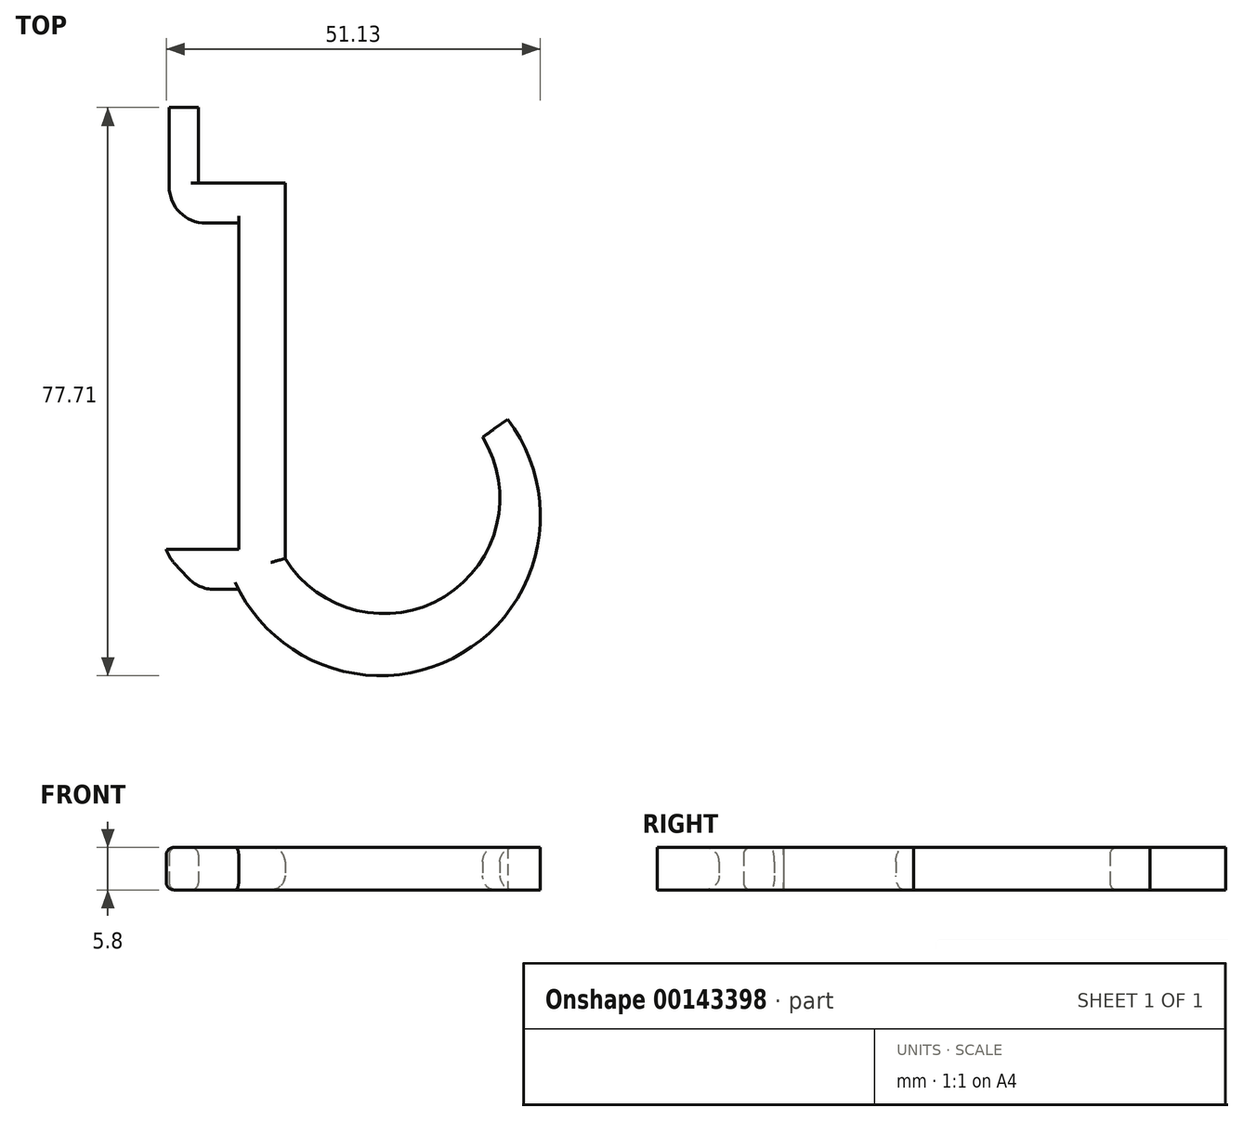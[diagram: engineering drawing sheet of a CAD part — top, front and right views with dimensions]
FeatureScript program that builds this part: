
annotation { "Feature Type Name" : "Feature", "Feature Type Description" : "" }
export const myFeature = defineFeature(function(context is Context, id is Id, definition is map)
    precondition{}
    {
        {
            var Q0;
            Q0=qCreatedBy(makeId("Top.planeOp"),FACE);
            var sketch = newSketch(context, id + "F0", { "sketchPlane" : qUnion([Q0])});
            skLineSegment(sketch, "E0.top", {"start": v(0, 55.6) * mm, "end": v(6.35, 55.6) * mm});
            skLineSegment(sketch, "E0.left", {"start": v(0, 0) * mm, "end": v(0, 55.6) * mm});
            skLineSegment(sketch, "E0.right", {"start": v(6.35, 4.23) * mm, "end": v(6.35, 55.6) * mm});
            skArc(sketch, "E1", {"start": v(0, 0) * mm, "mid": v(31.07, -8.42) * mm, "end": v(36.78, 23.26) * mm});
            skArc(sketch, "E2", {"start": v(6.35, 4.23) * mm, "mid": v(28.16, -0.98) * mm, "end": v(33.37, 20.82) * mm});
            skLineSegment(sketch, "E3", {"start": v(33.37, 20.82) * mm, "end": v(36.78, 23.26) * mm});
            skLineSegment(sketch, "E4", {"start": v(0, 55.6) * mm, "end": v(-5.5, 55.6) * mm});
            skPoint(sketch, "E5.start.orphan", {"position": v(-5.5, 50.1) * mm});
            skLineSegment(sketch, "E6", {"start": v(-5.5, 50.1) * mm, "end": v(0, 50.1) * mm});
            skLineSegment(sketch, "E7", {"start": v(0, 27.8) * mm, "end": v(33.38, 27.8) * mm, "construction": true});
            skLineSegment(sketch, "E8", {"start": v(33.38, 27.8) * mm, "end": v(-54.11, 27.8) * mm, "construction": true});
            skLineSegment(sketch, "E9.MirrorCS", {"start": v(0, 0) * mm, "end": v(-5.5, 0) * mm});
            skLineSegment(sketch, "E10.MirrorCS", {"start": v(-5.5, 5.5) * mm, "end": v(0, 5.5) * mm});
            skPoint(sketch, "E11.MirrorCS.end.orphan", {"position": v(-5.5, 5.5) * mm});
            skPoint(sketch, "E11.MirrorCS.start.orphan", {"position": v(-12.78, -1.43) * mm});
            skPoint(sketch, "E12.MirrorCS.start.orphan", {"position": v(-12.78, -7.8) * mm});
            skPoint(sketch, "E13.MirrorCS.start.orphan", {"position": v(-5.5, 0) * mm});
            skLineSegment(sketch, "E14", {"start": v(-5.5, 55.6) * mm, "end": v(-5.5, 65.91) * mm});
            skLineSegment(sketch, "E15", {"start": v(-5.5, 65.91) * mm, "end": v(-9.5, 65.91) * mm});
            skLineSegment(sketch, "E16", {"start": v(-9.5, 65.91) * mm, "end": v(-9.5, 50.1) * mm});
            skLineSegment(sketch, "E17", {"start": v(-9.5, 50.1) * mm, "end": v(-5.5, 50.1) * mm});
            skPoint(sketch, "E18.start.orphan", {"position": v(-12.78, 63.4) * mm});
            skPoint(sketch, "E19.start.orphan", {"position": v(-12.78, 57.03) * mm});
            skPoint(sketch, "E20.end.orphan", {"position": v(-26.56, 0) * mm});
            skLineSegment(sketch, "E21", {"start": v(0, 50.1) * mm, "end": v(0, 55.6) * mm, "construction": true});
            skLineSegment(sketch, "E22", {"start": v(0, 52.85) * mm, "end": v(-28.66, 52.85) * mm, "construction": true});
            skPoint(sketch, "E22.endSnap0", {"position": v(0, 52.85) * mm});
            skLineSegment(sketch, "E23", {"start": v(0, 5.5) * mm, "end": v(0, 0) * mm, "construction": true});
            skLineSegment(sketch, "E24", {"start": v(0, 2.75) * mm, "end": v(-28.66, 2.75) * mm, "construction": true});
            skLineSegment(sketch, "E25", {"start": v(-28.66, 2.75) * mm, "end": v(-28.66, 52.85) * mm, "construction": true});
            skLineSegment(sketch, "E26", {"start": v(-5.5, 5.5) * mm, "end": v(-5.5, 16.71) * mm});
            skLineSegment(sketch, "E27", {"start": v(-5.5, 16.71) * mm, "end": v(-10.12, 16.71) * mm});
            skLineSegment(sketch, "E28", {"start": v(-10.12, 16.71) * mm, "end": v(-10.12, 5) * mm});
            skLineSegment(sketch, "E29", {"start": v(-10.12, 5) * mm, "end": v(-5.5, 0) * mm});
            skSolve(sketch);
        }
        {
            var Q0;
            Q0 = qSketchRegion(id + "F0", true);
            extrude(context, id + "F1", {"entities" : qUnion([Q0]), "depth" : 5.8 * mm});
        }
        {
            var Q0;
            Q0=makeQuery(id+"F1.opExtrude","SWEPT_EDGE",EDGE,{"disambiguationData":[OSD([sQuery(id+"F0.wireOp",EDGE,"E16"),sQuery(id+"F0.wireOp",EDGE,"E17")])]});
            fillet(context, id + "F2", {"entities" : qUnion([Q0]), "radius" : 5 * mm, "tangentPropagation" : true, "allowEdgeOverflow" : false});
        }
        {
            var Q0;
            Q0=makeQuery(id+"F1.opExtrude","SWEPT_EDGE",EDGE,{"disambiguationData":[OSD([sQuery(id+"F0.wireOp",EDGE,"E28"),sQuery(id+"F0.wireOp",EDGE,"E29")])]});
            var Q1;
            Q1=makeQuery(id+"F1.opExtrude","SWEPT_EDGE",EDGE,{"disambiguationData":[OSD([sQuery(id+"F0.wireOp",EDGE,"E9.MirrorCS"),sQuery(id+"F0.wireOp",EDGE,"E29")])]});
            fillet(context, id + "F3", {"entities" : qUnion([Q0, Q1]), "radius" : 5 * mm, "tangentPropagation" : true, "allowEdgeOverflow" : false});
        }
        {
            var Q0;
            Q0=makeQuery(id+"F1.opExtrude","CAP_EDGE",EDGE,{"disambiguationData":[OSD([sQuery(id+"F0.wireOp",EDGE,"E0.right")])],"isStart":true});
            var Q1;
            Q1=makeQuery(id+"F1.opExtrude","CAP_EDGE",EDGE,{"disambiguationData":[OSD([sQuery(id+"F0.wireOp",EDGE,"E0.right")])],"isStart":false});
            var Q2;
            Q2=makeQuery(id+"F1.opExtrude","CAP_EDGE",EDGE,{"disambiguationData":[OSD([sQuery(id+"F0.wireOp",EDGE,"E2")])],"isStart":false});
            var Q3;
            Q3=makeQuery(id+"F1.opExtrude","CAP_EDGE",EDGE,{"disambiguationData":[OSD([sQuery(id+"F0.wireOp",EDGE,"E2")])],"isStart":true});
            fillet(context, id + "F4", {"entities" : qUnion([Q0, Q1, Q2, Q3]), "radius" : 1.96 * mm, "tangentPropagation" : true, "allowEdgeOverflow" : false});
        }
        {
            var Q0;
            Q0=makeQuery(id+"F1.opExtrude","CAP_EDGE",EDGE,{"disambiguationData":[OSD([sQuery(id+"F0.wireOp",EDGE,"E26")])],"isStart":false});
            var Q1;
            Q1=makeQuery(id+"F1.opExtrude","CAP_EDGE",EDGE,{"disambiguationData":[OSD([sQuery(id+"F0.wireOp",EDGE,"E26")])],"isStart":true});
            var Q2;
            Q2=makeQuery(id+"F1.opExtrude","CAP_EDGE",EDGE,{"disambiguationData":[OSD([sQuery(id+"F0.wireOp",EDGE,"E28")])],"isStart":false});
            var Q3;
            Q3=makeQuery(id+"F1.opExtrude","CAP_EDGE",EDGE,{"disambiguationData":[OSD([sQuery(id+"F0.wireOp",EDGE,"E28")])],"isStart":true});
            var Q4;
            {var subQ0=sQuery(id+"F0.wireOp",EDGE,"E29");var subQ1=sQuery(id+"F0.wireOp",EDGE,"E28");Q4=makeQuery(id+"F3.opFillet","BLEND_EDGE",EDGE,{"blendedFrom":[makeQuery(id+"F1.opExtrude","SWEPT_EDGE",EDGE,{"disambiguationData":[OSD([subQ1,subQ0])]}),makeQuery(id+"F1.opExtrude","CAP_FACE",FACE,{"disambiguationData":[OSD([sQuery(id+"F0.wireOp",EDGE,"E0.top"),sQuery(id+"F0.wireOp",EDGE,"E0.left"),sQuery(id+"F0.wireOp",EDGE,"E0.right"),sQuery(id+"F0.wireOp",EDGE,"E1"),sQuery(id+"F0.wireOp",EDGE,"E2"),sQuery(id+"F0.wireOp",EDGE,"E3"),sQuery(id+"F0.wireOp",EDGE,"E4"),sQuery(id+"F0.wireOp",EDGE,"E6"),sQuery(id+"F0.wireOp",EDGE,"E10.MirrorCS"),sQuery(id+"F0.wireOp",EDGE,"E9.MirrorCS"),sQuery(id+"F0.wireOp",EDGE,"E14"),sQuery(id+"F0.wireOp",EDGE,"E15"),sQuery(id+"F0.wireOp",EDGE,"E16"),sQuery(id+"F0.wireOp",EDGE,"E17"),sQuery(id+"F0.wireOp",EDGE,"E26"),sQuery(id+"F0.wireOp",EDGE,"E27"),subQ1,subQ0])],"isStart":true})],"blendedInto":[makeQuery(id+"F1.opExtrude","CAP_FACE",FACE,{"disambiguationData":[OSD([sQuery(id+"F0.wireOp",EDGE,"E0.top"),sQuery(id+"F0.wireOp",EDGE,"E0.left"),sQuery(id+"F0.wireOp",EDGE,"E0.right"),sQuery(id+"F0.wireOp",EDGE,"E1"),sQuery(id+"F0.wireOp",EDGE,"E2"),sQuery(id+"F0.wireOp",EDGE,"E3"),sQuery(id+"F0.wireOp",EDGE,"E4"),sQuery(id+"F0.wireOp",EDGE,"E6"),sQuery(id+"F0.wireOp",EDGE,"E10.MirrorCS"),sQuery(id+"F0.wireOp",EDGE,"E9.MirrorCS"),sQuery(id+"F0.wireOp",EDGE,"E14"),sQuery(id+"F0.wireOp",EDGE,"E15"),sQuery(id+"F0.wireOp",EDGE,"E16"),sQuery(id+"F0.wireOp",EDGE,"E17"),sQuery(id+"F0.wireOp",EDGE,"E26"),sQuery(id+"F0.wireOp",EDGE,"E27"),subQ1,subQ0])],"isStart":true})]});}
            var Q5;
            {var subQ0=sQuery(id+"F0.wireOp",EDGE,"E29");var subQ1=sQuery(id+"F0.wireOp",EDGE,"E28");Q5=makeQuery(id+"F3.opFillet","BLEND_EDGE",EDGE,{"blendedFrom":[makeQuery(id+"F1.opExtrude","SWEPT_EDGE",EDGE,{"disambiguationData":[OSD([subQ1,subQ0])]}),makeQuery(id+"F1.opExtrude","CAP_FACE",FACE,{"disambiguationData":[OSD([sQuery(id+"F0.wireOp",EDGE,"E0.top"),sQuery(id+"F0.wireOp",EDGE,"E0.left"),sQuery(id+"F0.wireOp",EDGE,"E0.right"),sQuery(id+"F0.wireOp",EDGE,"E1"),sQuery(id+"F0.wireOp",EDGE,"E2"),sQuery(id+"F0.wireOp",EDGE,"E3"),sQuery(id+"F0.wireOp",EDGE,"E4"),sQuery(id+"F0.wireOp",EDGE,"E6"),sQuery(id+"F0.wireOp",EDGE,"E10.MirrorCS"),sQuery(id+"F0.wireOp",EDGE,"E9.MirrorCS"),sQuery(id+"F0.wireOp",EDGE,"E14"),sQuery(id+"F0.wireOp",EDGE,"E15"),sQuery(id+"F0.wireOp",EDGE,"E16"),sQuery(id+"F0.wireOp",EDGE,"E17"),sQuery(id+"F0.wireOp",EDGE,"E26"),sQuery(id+"F0.wireOp",EDGE,"E27"),subQ1,subQ0])],"isStart":false})],"blendedInto":[makeQuery(id+"F1.opExtrude","CAP_FACE",FACE,{"disambiguationData":[OSD([sQuery(id+"F0.wireOp",EDGE,"E0.top"),sQuery(id+"F0.wireOp",EDGE,"E0.left"),sQuery(id+"F0.wireOp",EDGE,"E0.right"),sQuery(id+"F0.wireOp",EDGE,"E1"),sQuery(id+"F0.wireOp",EDGE,"E2"),sQuery(id+"F0.wireOp",EDGE,"E3"),sQuery(id+"F0.wireOp",EDGE,"E4"),sQuery(id+"F0.wireOp",EDGE,"E6"),sQuery(id+"F0.wireOp",EDGE,"E10.MirrorCS"),sQuery(id+"F0.wireOp",EDGE,"E9.MirrorCS"),sQuery(id+"F0.wireOp",EDGE,"E14"),sQuery(id+"F0.wireOp",EDGE,"E15"),sQuery(id+"F0.wireOp",EDGE,"E16"),sQuery(id+"F0.wireOp",EDGE,"E17"),sQuery(id+"F0.wireOp",EDGE,"E26"),sQuery(id+"F0.wireOp",EDGE,"E27"),subQ1,subQ0])],"isStart":false})]});}
            var Q6;
            Q6=makeQuery(id+"F1.opExtrude","CAP_EDGE",EDGE,{"disambiguationData":[OSD([sQuery(id+"F0.wireOp",EDGE,"E16")])],"isStart":true});
            var Q7;
            Q7=makeQuery(id+"F1.opExtrude","CAP_EDGE",EDGE,{"disambiguationData":[OSD([sQuery(id+"F0.wireOp",EDGE,"E16")])],"isStart":false});
            var Q8;
            Q8=makeQuery(id+"F1.opExtrude","CAP_EDGE",EDGE,{"disambiguationData":[OSD([sQuery(id+"F0.wireOp",EDGE,"E14")])],"isStart":true});
            var Q9;
            Q9=makeQuery(id+"F1.opExtrude","CAP_EDGE",EDGE,{"disambiguationData":[OSD([sQuery(id+"F0.wireOp",EDGE,"E14")])],"isStart":false});
            fillet(context, id + "F5", {"entities" : qUnion([Q0, Q1, Q2, Q3, Q4, Q5, Q6, Q7, Q8, Q9]), "radius" : 1 * mm, "tangentPropagation" : true, "allowEdgeOverflow" : false});
        }
        {
            var Q0;
            Q0=makeQuery(id+"F1.opExtrude","CAP_FACE",FACE,{"disambiguationData":[OSD([sQuery(id+"F0.wireOp",EDGE,"E0.top"),sQuery(id+"F0.wireOp",EDGE,"E0.left"),sQuery(id+"F0.wireOp",EDGE,"E0.right"),sQuery(id+"F0.wireOp",EDGE,"E1"),sQuery(id+"F0.wireOp",EDGE,"E2"),sQuery(id+"F0.wireOp",EDGE,"E3"),sQuery(id+"F0.wireOp",EDGE,"E4"),sQuery(id+"F0.wireOp",EDGE,"E6"),sQuery(id+"F0.wireOp",EDGE,"E10.MirrorCS"),sQuery(id+"F0.wireOp",EDGE,"E9.MirrorCS"),sQuery(id+"F0.wireOp",EDGE,"E14"),sQuery(id+"F0.wireOp",EDGE,"E15"),sQuery(id+"F0.wireOp",EDGE,"E16"),sQuery(id+"F0.wireOp",EDGE,"E17"),sQuery(id+"F0.wireOp",EDGE,"E26"),sQuery(id+"F0.wireOp",EDGE,"E27"),sQuery(id+"F0.wireOp",EDGE,"E28"),sQuery(id+"F0.wireOp",EDGE,"E29")])],"isStart":false});
            var sketch = newSketch(context, id + "F6", { "sketchPlane" : qUnion([Q0])});
            skLineSegment(sketch, "E30.bottom", {"start": v(-5.38, 5.5) * mm, "end": v(-13.14, 5.5) * mm});
            skLineSegment(sketch, "E30.top", {"start": v(-5.38, 17.8) * mm, "end": v(-13.14, 17.8) * mm});
            skLineSegment(sketch, "E30.left", {"start": v(-5.38, 5.5) * mm, "end": v(-5.38, 17.8) * mm});
            skLineSegment(sketch, "E30.right", {"start": v(-13.14, 5.5) * mm, "end": v(-13.14, 17.8) * mm});
            skSolve(sketch);
        }
        {
            var Q0;
            Q0=makeQuery(id+"F6.imprint","IMPRINT",FACE,{"disambiguationData":[TD([[makeQuery(id+"F6.imprint","IMPRINT",EDGE,{"derivedFrom":sQuery(id+"F6.wireOp",EDGE,"E30.top")}),1.0]])]});
            var Q1;
            {var subQ2=sQuery(id+"F0.wireOp",EDGE,"E27");Q1=makeQuery(id+"F6.imprint","IMPRINT",FACE,{"disambiguationData":[TD([[makeQuery(id+"F6.imprint","IMPRINT",EDGE,{"derivedFrom":makeQuery(id+"F1.opExtrude","CAP_EDGE",EDGE,{"disambiguationData":[OSD([subQ2])],"isStart":false})}),1.0]])]});}
            extrude(context, id + "F7", {"entities" : qUnion([Q0, Q1]), "operationType" : NewBodyOperationType.REMOVE, "endBound" : BoundingType.THROUGH_ALL, "oppositeDirection" : true, "depth" : 25 * mm, "hasSecondDirection" : true, "secondDirectionOppositeDirection" : false, "secondDirectionDepth" : 25 * mm});
        }
    });
